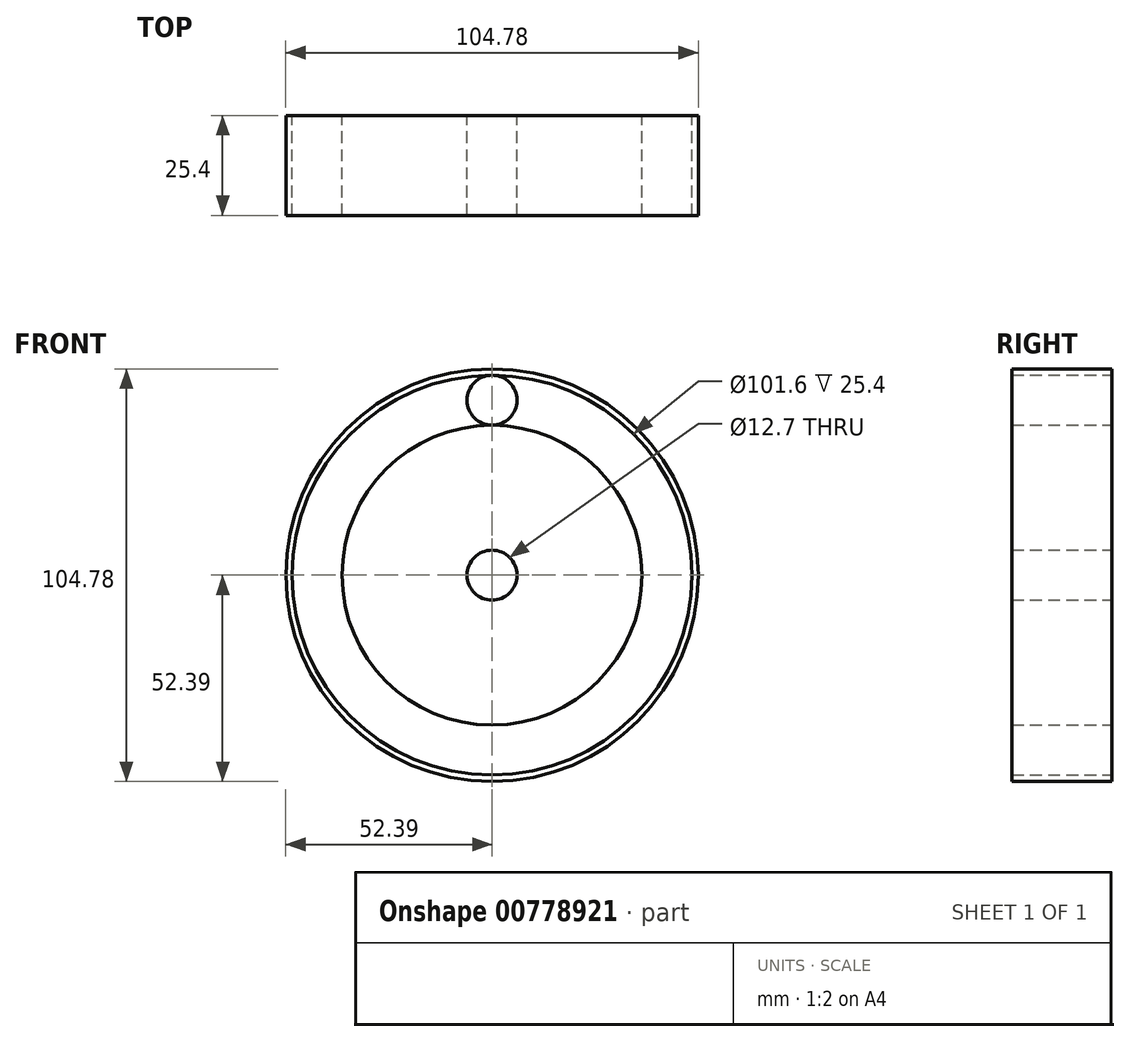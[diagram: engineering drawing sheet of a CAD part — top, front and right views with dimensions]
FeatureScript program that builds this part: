
annotation { "Feature Type Name" : "Feature", "Feature Type Description" : "" }
export const myFeature = defineFeature(function(context is Context, id is Id, definition is map)
    precondition{}
    {
        {
            var Q0;
            Q0=qCreatedBy(makeId("Front.planeOp"),FACE);
            var sketch = newSketch(context, id + "F0", { "sketchPlane" : qUnion([Q0])});
            skCircle(sketch, "E0", {"center": v(0, 0) * mm, "radius": 38.1 * mm});
            skCircle(sketch, "E1", {"center": v(0, 0) * mm, "radius": 50.8 * mm});
            skCircle(sketch, "E2", {"center": v(0, 44.45) * mm, "radius": 6.35 * mm});
            skCircle(sketch, "E3.0", {"center": v(0, 0) * mm, "radius": 52.39 * mm});
            skCircle(sketch, "E4.0", {"center": v(0, 0) * mm, "radius": 36.51 * mm});
            skLineSegment(sketch, "E5", {"start": v(-36.51, 0) * mm, "end": v(36.51, 0) * mm});
            skCircle(sketch, "E6", {"center": v(0, 0) * mm, "radius": 6.35 * mm});
            skCircle(sketch, "E7", {"center": v(0, 0) * mm, "radius": 3.18 * mm});
            skSolve(sketch);
        }
        {
            var Q0;
            Q0=makeQuery(id+"F0.imprint","IMPRINT",FACE,{"disambiguationData":[TD([[makeQuery(id+"F0.imprint","IMPRINT",EDGE,{"derivedFrom":sQuery(id+"F0.wireOp",EDGE,"E1")}),-1.0]])]});
            extrude(context, id + "F1", {"entities" : qUnion([Q0]), "depth" : 25.4 * mm, "offsetDistance" : 25.4 * mm});
        }
        {
            var Q0;
            {var subQ0=sQuery(id+"F0.wireOp",EDGE,"E2");var subQ1=makeQuery(id+"F0.imprint","INTERSECT",VERTEX,{"derivedFrom":[sQuery(id+"F0.wireOp",EDGE,"E0"),subQ0]});Q0=makeQuery(id+"F0.imprint","IMPRINT",FACE,{"disambiguationData":[TD([[makeQuery(id+"F0.imprint","IMPRINT",EDGE,{"disambiguationData":[TD([[subQ1,1.0]])],"derivedFrom":subQ0}),1.0]])]});}
            extrude(context, id + "F2", {"entities" : qUnion([Q0]), "operationType" : NewBodyOperationType.ADD, "depth" : 25.4 * mm, "offsetDistance" : 25.4 * mm});
        }
        {
            var Q0;
            {var subQ0=sQuery(id+"F0.wireOp",EDGE,"E6");var subQ1=sQuery(id+"F0.wireOp",EDGE,"E5");var subQ2=makeQuery(id+"F0.imprint","INTERSECT",VERTEX,{"disambiguationData":[OD(0.0)],"derivedFrom":[subQ1,subQ0]});Q0=makeQuery(id+"F0.imprint","IMPRINT",FACE,{"disambiguationData":[TD([[makeQuery(id+"F0.imprint","IMPRINT",EDGE,{"disambiguationData":[TD([[subQ2,-1.0]])],"derivedFrom":subQ1}),-1.0]])]});}
            var Q1;
            Q1=makeQuery(id+"F0.imprint","IMPRINT",FACE,{"disambiguationData":[TD([[makeQuery(id+"F0.imprint","IMPRINT",EDGE,{"derivedFrom":sQuery(id+"F0.wireOp",EDGE,"E0")}),1.0]])]});
            var Q2;
            {var subQ0=sQuery(id+"F0.wireOp",EDGE,"E5");var subQ1=sQuery(id+"F0.wireOp",EDGE,"E4.0");var subQ2=makeQuery(id+"F0.imprint","INTERSECT",VERTEX,{"disambiguationData":[OD(0.0)],"derivedFrom":[subQ1,subQ0]});Q2=makeQuery(id+"F0.imprint","IMPRINT",FACE,{"disambiguationData":[TD([[makeQuery(id+"F0.imprint","IMPRINT",EDGE,{"disambiguationData":[TD([[subQ2,-1.0]])],"derivedFrom":subQ1}),1.0]])]});}
            var Q3;
            {var subQ0=sQuery(id+"F0.wireOp",EDGE,"E6");var subQ1=sQuery(id+"F0.wireOp",EDGE,"E5");var subQ2=makeQuery(id+"F0.imprint","INTERSECT",VERTEX,{"disambiguationData":[OD(0.0)],"derivedFrom":[subQ1,subQ0]});Q3=makeQuery(id+"F0.imprint","IMPRINT",FACE,{"disambiguationData":[TD([[makeQuery(id+"F0.imprint","IMPRINT",EDGE,{"disambiguationData":[TD([[subQ2,-1.0]])],"derivedFrom":subQ1}),1.0]])]});}
            extrude(context, id + "F3", {"entities" : qUnion([Q0, Q1, Q2, Q3]), "operationType" : NewBodyOperationType.ADD, "depth" : 25.4 * mm, "offsetDistance" : 25.4 * mm});
        }
        {
            var Q0;
            Q0=makeQuery(id+"F0.imprint","IMPRINT",FACE,{"disambiguationData":[TD([[makeQuery(id+"F0.imprint","IMPRINT",EDGE,{"derivedFrom":sQuery(id+"F0.wireOp",EDGE,"E0")}),1.0]])]});
            var Q1;
            {var subQ0=sQuery(id+"F0.wireOp",EDGE,"E5");var subQ1=sQuery(id+"F0.wireOp",EDGE,"E4.0");var subQ2=makeQuery(id+"F0.imprint","INTERSECT",VERTEX,{"disambiguationData":[OD(0.0)],"derivedFrom":[subQ1,subQ0]});Q1=makeQuery(id+"F0.imprint","IMPRINT",FACE,{"disambiguationData":[TD([[makeQuery(id+"F0.imprint","IMPRINT",EDGE,{"disambiguationData":[TD([[subQ2,-1.0]])],"derivedFrom":subQ1}),1.0]])]});}
            var Q2;
            {var subQ0=sQuery(id+"F0.wireOp",EDGE,"E6");var subQ1=sQuery(id+"F0.wireOp",EDGE,"E5");var subQ2=makeQuery(id+"F0.imprint","INTERSECT",VERTEX,{"disambiguationData":[OD(0.0)],"derivedFrom":[subQ1,subQ0]});Q2=makeQuery(id+"F0.imprint","IMPRINT",FACE,{"disambiguationData":[TD([[makeQuery(id+"F0.imprint","IMPRINT",EDGE,{"disambiguationData":[TD([[subQ2,-1.0]])],"derivedFrom":subQ1}),1.0]])]});}
            var Q3;
            {var subQ0=sQuery(id+"F0.wireOp",EDGE,"E6");var subQ1=sQuery(id+"F0.wireOp",EDGE,"E5");var subQ2=makeQuery(id+"F0.imprint","INTERSECT",VERTEX,{"disambiguationData":[OD(0.0)],"derivedFrom":[subQ1,subQ0]});Q3=makeQuery(id+"F0.imprint","IMPRINT",FACE,{"disambiguationData":[TD([[makeQuery(id+"F0.imprint","IMPRINT",EDGE,{"disambiguationData":[TD([[subQ2,-1.0]])],"derivedFrom":subQ1}),-1.0]])]});}
            extrude(context, id + "F4", {"entities" : qUnion([Q0, Q1, Q2, Q3]), "operationType" : NewBodyOperationType.ADD, "depth" : 25.4 * mm, "offsetDistance" : 25.4 * mm});
        }
    });
